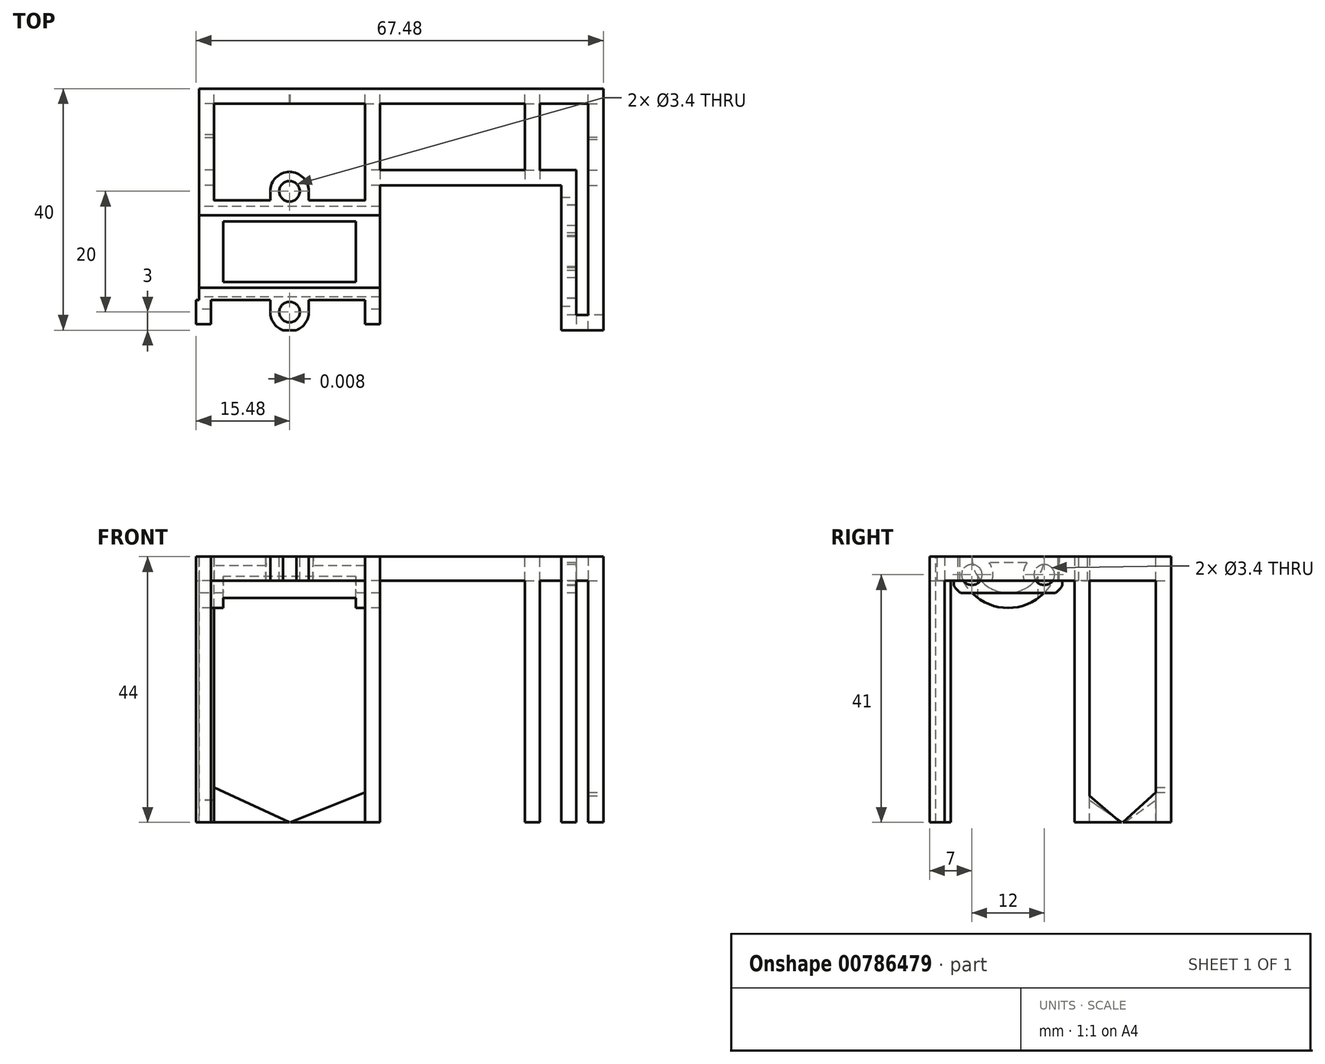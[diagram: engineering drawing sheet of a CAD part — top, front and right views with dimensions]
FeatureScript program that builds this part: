
annotation { "Feature Type Name" : "Feature", "Feature Type Description" : "" }
export const myFeature = defineFeature(function(context is Context, id is Id, definition is map)
    precondition{}
    {
        {
            var Q0;
            Q0=qCreatedBy(makeId("Top.planeOp"),FACE);
            var sketch = newSketch(context, id + "F0", { "sketchPlane" : qUnion([Q0])});
            skLineSegment(sketch, "E0.bottom", {"start": v(-33.5, 20) * mm, "end": v(33.5, 20) * mm});
            skLineSegment(sketch, "E0.top", {"start": v(-33.5, -20) * mm, "end": v(-3.5, -20) * mm});
            skLineSegment(sketch, "E0.left", {"start": v(-33.5, 20) * mm, "end": v(-33.5, -20) * mm});
            skLineSegment(sketch, "E0.right", {"start": v(33.5, 20) * mm, "end": v(33.5, -20) * mm});
            skLineSegment(sketch, "E1.top", {"start": v(-3.5, 4) * mm, "end": v(26.5, 4) * mm});
            skLineSegment(sketch, "E1.left", {"start": v(-3.5, -20) * mm, "end": v(-3.5, 4) * mm});
            skLineSegment(sketch, "E1.right", {"start": v(26.5, -20) * mm, "end": v(26.5, 4) * mm});
            skLineSegment(sketch, "E2.trimOffspring", {"start": v(26.5, -20) * mm, "end": v(33.5, -20) * mm});
            skSolve(sketch);
        }
        {
            var Q0;
            Q0 = qSketchRegion(id + "F0", true);
            extrude(context, id + "F1", {"entities" : qUnion([Q0]), "depth" : 4 * mm, "offsetDistance" : 25 * mm});
        }
        {
            var Q0;
            Q0=makeQuery(id+"F1.opExtrude","SWEPT_FACE",FACE,{"disambiguationData":[OSD([sQuery(id+"F0.wireOp",EDGE,"E0.left")])]});
            var sketch = newSketch(context, id + "F2", { "sketchPlane" : qUnion([Q0])});
            skArc(sketch, "E3", {"start": v(1, 4) * mm, "mid": v(7, -2) * mm, "end": v(13, 4) * mm});
            skArc(sketch, "E4", {"start": v(-1.5, 4) * mm, "mid": v(7, -4.5) * mm, "end": v(15.5, 4) * mm});
            skLineSegment(sketch, "E5", {"start": v(-1.5, 4) * mm, "end": v(15.5, 4) * mm});
            skSolve(sketch);
        }
        {
            var Q0;
            {var subQ0=sQuery(id+"F2.wireOp",EDGE,"E3");var subQ1=makeQuery(id+"F1.opExtrude","CAP_EDGE",EDGE,{"disambiguationData":[OSD([sQuery(id+"F0.wireOp",EDGE,"E0.left")])],"isStart":true});var subQ2=makeQuery(id+"F2.imprint","INTERSECT",VERTEX,{"disambiguationData":[OD(0.0)],"derivedFrom":[subQ1,subQ0]});Q0=makeQuery(id+"F2.imprint","IMPRINT",FACE,{"disambiguationData":[TD([[makeQuery(id+"F2.imprint","IMPRINT",EDGE,{"disambiguationData":[TD([[subQ2,-1.0]])],"derivedFrom":subQ0}),-1.0]])]});}
            extrude(context, id + "F3", {"entities" : qUnion([Q0]), "operationType" : NewBodyOperationType.ADD, "oppositeDirection" : true, "depth" : 30 * mm, "offsetDistance" : 25 * mm});
        }
        {
            var Q0;
            {var subQ0=sQuery(id+"F2.wireOp",EDGE,"E5");var subQ1=sQuery(id+"F2.wireOp",EDGE,"E3");var subQ2=makeQuery(id+"F2.imprint","INTERSECT",VERTEX,{"disambiguationData":[OD(0.0)],"derivedFrom":[subQ1,subQ0]});Q0=makeQuery(id+"F2.imprint","IMPRINT",FACE,{"disambiguationData":[TD([[makeQuery(id+"F2.imprint","IMPRINT",EDGE,{"disambiguationData":[TD([[subQ2,-1.0]])],"derivedFrom":subQ1}),1.0]])]});}
            extrude(context, id + "F4", {"entities" : qUnion([Q0]), "operationType" : NewBodyOperationType.REMOVE, "oppositeDirection" : true, "depth" : 30 * mm, "offsetDistance" : 25 * mm});
        }
        {
            var Q0;
            {var subQ0=sQuery(id+"F0.wireOp",EDGE,"E1.left");var subQ1=sQuery(id+"F0.wireOp",EDGE,"E0.left");var subQ5=sQuery(id+"F0.wireOp",EDGE,"E0.top");Q0=makeQuery(id+"F4.boolean.opBoolean","SPLIT",FACE,{"disambiguationData":[TD([makeQuery(id+"F1.opExtrude","SWEPT_FACE",FACE,{"disambiguationData":[OSD([subQ5])]})])],"derivedFrom":makeQuery(id+"F1.opExtrude","CAP_FACE",FACE,{"disambiguationData":[OSD([sQuery(id+"F0.wireOp",EDGE,"E0.bottom"),subQ5,subQ1,sQuery(id+"F0.wireOp",EDGE,"E0.right"),sQuery(id+"F0.wireOp",EDGE,"E1.top"),subQ0,sQuery(id+"F0.wireOp",EDGE,"E1.right"),sQuery(id+"F0.wireOp",EDGE,"E2.trimOffspring")])],"isStart":false})});}
            var sketch = newSketch(context, id + "F5", { "sketchPlane" : qUnion([Q0])});
            skCircle(sketch, "E6", {"center": v(-18.5, -17) * mm, "radius": 1.7 * mm});
            skSolve(sketch);
        }
        {
            var Q0;
            Q0 = qSketchRegion(id + "F5", true);
            extrude(context, id + "F6", {"entities" : qUnion([Q0]), "operationType" : NewBodyOperationType.REMOVE, "oppositeDirection" : true, "depth" : 4 * mm, "offsetDistance" : 25 * mm});
        }
        {
            var Q0;
            {var subQ2=sQuery(id+"F0.wireOp",EDGE,"E0.left");var subQ3=sQuery(id+"F0.wireOp",EDGE,"E1.top");var subQ4=sQuery(id+"F0.wireOp",EDGE,"E0.right");var subQ5=sQuery(id+"F0.wireOp",EDGE,"E2.trimOffspring");var subQ6=sQuery(id+"F0.wireOp",EDGE,"E1.right");var subQ7=sQuery(id+"F0.wireOp",EDGE,"E1.left");var subQ8=sQuery(id+"F0.wireOp",EDGE,"E0.bottom");Q0=makeQuery(id+"F4.boolean.opBoolean","SPLIT",FACE,{"disambiguationData":[TD([makeQuery(id+"F1.opExtrude","SWEPT_FACE",FACE,{"disambiguationData":[OSD([subQ8])]})])],"derivedFrom":makeQuery(id+"F1.opExtrude","CAP_FACE",FACE,{"disambiguationData":[OSD([subQ8,sQuery(id+"F0.wireOp",EDGE,"E0.top"),subQ2,subQ4,subQ3,subQ7,subQ6,subQ5])],"isStart":false})});}
            var sketch = newSketch(context, id + "F7", { "sketchPlane" : qUnion([Q0])});
            skCircle(sketch, "E7", {"center": v(-18.5, 3) * mm, "radius": 1.7 * mm});
            skSolve(sketch);
        }
        {
            var Q0;
            Q0 = qSketchRegion(id + "F7", true);
            extrude(context, id + "F8", {"entities" : qUnion([Q0]), "operationType" : NewBodyOperationType.REMOVE, "endBound" : BoundingType.THROUGH_ALL, "oppositeDirection" : true, "depth" : 70 * mm, "offsetDistance" : 25 * mm});
        }
        {
            var Q0;
            {var subQ2=sQuery(id+"F0.wireOp",EDGE,"E0.left");var subQ3=sQuery(id+"F0.wireOp",EDGE,"E1.top");var subQ4=sQuery(id+"F0.wireOp",EDGE,"E0.right");var subQ5=sQuery(id+"F0.wireOp",EDGE,"E2.trimOffspring");var subQ6=sQuery(id+"F0.wireOp",EDGE,"E1.right");var subQ7=sQuery(id+"F0.wireOp",EDGE,"E1.left");var subQ8=sQuery(id+"F0.wireOp",EDGE,"E0.bottom");Q0=makeQuery(id+"F4.boolean.opBoolean","SPLIT",FACE,{"disambiguationData":[TD([makeQuery(id+"F1.opExtrude","SWEPT_FACE",FACE,{"disambiguationData":[OSD([subQ8])]})])],"derivedFrom":makeQuery(id+"F1.opExtrude","CAP_FACE",FACE,{"disambiguationData":[OSD([subQ8,sQuery(id+"F0.wireOp",EDGE,"E0.top"),subQ2,subQ4,subQ3,subQ7,subQ6,subQ5])],"isStart":false})});}
            shell(context, id + "F9", {"entities" : qUnion([Q0]), "thickness" : 2.5 * mm});
        }
        {
            var Q0;
            Q0=makeQuery(id+"F9.opShell","OFFSET_FACE",FACE,{"disambiguationData":[OSD([sQuery(id+"F0.wireOp",EDGE,"E0.bottom"),sQuery(id+"F0.wireOp",EDGE,"E0.top"),sQuery(id+"F0.wireOp",EDGE,"E0.left"),sQuery(id+"F0.wireOp",EDGE,"E0.right"),sQuery(id+"F0.wireOp",EDGE,"E1.top"),sQuery(id+"F0.wireOp",EDGE,"E1.left"),sQuery(id+"F0.wireOp",EDGE,"E1.right"),sQuery(id+"F0.wireOp",EDGE,"E2.trimOffspring")])]});
            extrude(context, id + "F10", {"entities" : qUnion([Q0]), "operationType" : NewBodyOperationType.REMOVE, "oppositeDirection" : true, "depth" : 3 * mm, "offsetDistance" : 25 * mm});
        }
        {
            var Q0;
            {var subQ0=sQuery(id+"F0.wireOp",EDGE,"E1.left");var subQ1=sQuery(id+"F0.wireOp",EDGE,"E0.left");var subQ5=sQuery(id+"F0.wireOp",EDGE,"E0.top");Q0=makeQuery(id+"F4.boolean.opBoolean","SPLIT",FACE,{"disambiguationData":[TD([makeQuery(id+"F1.opExtrude","SWEPT_FACE",FACE,{"disambiguationData":[OSD([subQ5])]})])],"derivedFrom":makeQuery(id+"F1.opExtrude","CAP_FACE",FACE,{"disambiguationData":[OSD([sQuery(id+"F0.wireOp",EDGE,"E0.bottom"),subQ5,subQ1,sQuery(id+"F0.wireOp",EDGE,"E0.right"),sQuery(id+"F0.wireOp",EDGE,"E1.top"),subQ0,sQuery(id+"F0.wireOp",EDGE,"E1.right"),sQuery(id+"F0.wireOp",EDGE,"E2.trimOffspring")])],"isStart":false})});}
            var sketch = newSketch(context, id + "F11", { "sketchPlane" : qUnion([Q0])});
            skLineSegment(sketch, "E8.bottom", {"start": v(-7.5, -2) * mm, "end": v(-29.5, -2) * mm});
            skLineSegment(sketch, "E8.top", {"start": v(-7.5, -12) * mm, "end": v(-29.5, -12) * mm});
            skLineSegment(sketch, "E8.left", {"start": v(-7.5, -2) * mm, "end": v(-7.5, -12) * mm});
            skLineSegment(sketch, "E8.right", {"start": v(-29.5, -2) * mm, "end": v(-29.5, -12) * mm});
            skSolve(sketch);
        }
        {
            var Q0;
            Q0 = qSketchRegion(id + "F11", true);
            extrude(context, id + "F12", {"entities" : qUnion([Q0]), "operationType" : NewBodyOperationType.REMOVE, "oppositeDirection" : true, "depth" : 9 * mm, "offsetDistance" : 25 * mm});
        }
        {
            var Q0;
            Q0=makeQuery(id+"F1.opExtrude","SWEPT_FACE",FACE,{"disambiguationData":[OSD([sQuery(id+"F0.wireOp",EDGE,"E1.right")])]});
            var sketch = newSketch(context, id + "F13", { "sketchPlane" : qUnion([Q0])});
            skLineSegment(sketch, "E9.bottom", {"start": v(16, -3) * mm, "end": v(-2, -3) * mm});
            skLineSegment(sketch, "E9.top", {"start": v(16, 7) * mm, "end": v(-2, 7) * mm});
            skLineSegment(sketch, "E9.left", {"start": v(16, -3) * mm, "end": v(16, 7) * mm});
            skLineSegment(sketch, "E9.right", {"start": v(-2, -3) * mm, "end": v(-2, 7) * mm});
            skSolve(sketch);
        }
        {
            var Q0;
            Q0 = qSketchRegion(id + "F13", true);
            extrude(context, id + "F14", {"entities" : qUnion([Q0]), "operationType" : NewBodyOperationType.ADD, "oppositeDirection" : true, "depth" : 2.5 * mm, "offsetDistance" : 25 * mm});
        }
        {
            var Q0;
            Q0=makeQuery(id+"F14.boolean.opBoolean","MERGE",FACE,{"derivedFrom":[makeQuery(id+"F1.opExtrude","SWEPT_FACE",FACE,{"disambiguationData":[OSD([sQuery(id+"F0.wireOp",EDGE,"E1.right")])]}),makeQuery(id+"F14.opExtrude","CAP_FACE",FACE,{"disambiguationData":[OSD([sQuery(id+"F13.wireOp",EDGE,"E9.bottom"),sQuery(id+"F13.wireOp",EDGE,"E9.top"),sQuery(id+"F13.wireOp",EDGE,"E9.left"),sQuery(id+"F13.wireOp",EDGE,"E9.right")])],"isStart":true})]});
            var sketch = newSketch(context, id + "F15", { "sketchPlane" : qUnion([Q0])});
            skCircle(sketch, "E10", {"center": v(1, 1) * mm, "radius": 1.7 * mm});
            skCircle(sketch, "E11", {"center": v(13, 1) * mm, "radius": 1.7 * mm});
            skLineSegment(sketch, "E12.bottom", {"start": v(-2, 4) * mm, "end": v(16, 4) * mm});
            skLineSegment(sketch, "E12.top", {"start": v(-2, 7) * mm, "end": v(16, 7) * mm});
            skLineSegment(sketch, "E12.left", {"start": v(-2, 4) * mm, "end": v(-2, 7) * mm});
            skLineSegment(sketch, "E12.right", {"start": v(16, 4) * mm, "end": v(16, 7) * mm});
            skSolve(sketch);
        }
        {
            var Q0;
            Q0 = qSketchRegion(id + "F15", true);
            extrude(context, id + "F16", {"entities" : qUnion([Q0]), "operationType" : NewBodyOperationType.REMOVE, "oppositeDirection" : true, "depth" : 2.5 * mm, "offsetDistance" : 25 * mm});
        }
        {
            var Q0;
            Q0=makeQuery(id+"F14.boolean.opBoolean","MERGE",FACE,{"derivedFrom":[makeQuery(id+"F1.opExtrude","SWEPT_FACE",FACE,{"disambiguationData":[OSD([sQuery(id+"F0.wireOp",EDGE,"E1.right")])]}),makeQuery(id+"F14.opExtrude","CAP_FACE",FACE,{"disambiguationData":[OSD([sQuery(id+"F13.wireOp",EDGE,"E9.bottom"),sQuery(id+"F13.wireOp",EDGE,"E9.top"),sQuery(id+"F13.wireOp",EDGE,"E9.left"),sQuery(id+"F13.wireOp",EDGE,"E9.right")])],"isStart":true})]});
            var sketch = newSketch(context, id + "F17", { "sketchPlane" : qUnion([Q0])});
            skCircle(sketch, "E13", {"center": v(1, 1) * mm, "radius": 3.5 * mm});
            skCircle(sketch, "E14", {"center": v(13, 1) * mm, "radius": 3.5 * mm});
            skLineSegment(sketch, "E15", {"start": v(1, -2.5) * mm, "end": v(13, -2.5) * mm});
            skLineSegment(sketch, "E16", {"start": v(1, 4.5) * mm, "end": v(13, 4.5) * mm});
            skLineSegment(sketch, "E17", {"start": v(-2, 3) * mm, "end": v(-1.87, 3) * mm});
            skLineSegment(sketch, "E18", {"start": v(-2.35, 0) * mm, "end": v(-2, 0) * mm});
            skLineSegment(sketch, "E19", {"start": v(16.1, 3) * mm, "end": v(15.88, 2.99) * mm});
            skLineSegment(sketch, "E20", {"start": v(16.35, 0) * mm, "end": v(16, 0) * mm});
            skLineSegment(sketch, "E21", {"start": v(4.35, 0) * mm, "end": v(9.65, 0) * mm});
            skLineSegment(sketch, "E22", {"start": v(3.87, 3) * mm, "end": v(10.13, 3) * mm});
            skSolve(sketch);
        }
        {
            var Q0;
            {var subQ0=sQuery(id+"F17.wireOp",EDGE,"E15");Q0=makeQuery(id+"F17.imprint","IMPRINT",FACE,{"disambiguationData":[TD([[makeQuery(id+"F17.imprint","IMPRINT",EDGE,{"derivedFrom":subQ0}),-1.0]])]});}
            var Q1;
            {var subQ1=sQuery(id+"F17.wireOp",EDGE,"E16");Q1=makeQuery(id+"F17.imprint","IMPRINT",FACE,{"disambiguationData":[TD([[makeQuery(id+"F17.imprint","IMPRINT",EDGE,{"derivedFrom":subQ1}),1.0]])]});}
            var Q2;
            {var subQ0=sQuery(id+"F17.wireOp",EDGE,"E21");Q2=makeQuery(id+"F17.imprint","IMPRINT",FACE,{"disambiguationData":[TD([[makeQuery(id+"F17.imprint","IMPRINT",EDGE,{"derivedFrom":subQ0}),1.0]])]});}
            extrude(context, id + "F18", {"entities" : qUnion([Q0, Q1, Q2]), "operationType" : NewBodyOperationType.REMOVE, "oppositeDirection" : true, "depth" : 2.5 * mm, "offsetDistance" : 25 * mm});
        }
        {
            var Q0;
            {var subQ2=sQuery(id+"F0.wireOp",EDGE,"E0.left");var subQ3=sQuery(id+"F0.wireOp",EDGE,"E1.top");var subQ4=sQuery(id+"F0.wireOp",EDGE,"E0.right");var subQ5=sQuery(id+"F0.wireOp",EDGE,"E2.trimOffspring");var subQ6=sQuery(id+"F0.wireOp",EDGE,"E1.right");var subQ7=sQuery(id+"F0.wireOp",EDGE,"E1.left");var subQ8=sQuery(id+"F0.wireOp",EDGE,"E0.bottom");Q0=makeQuery(id+"F18.boolean.opBoolean","MERGE",FACE,{"derivedFrom":[makeQuery(id+"F4.boolean.opBoolean","SPLIT",FACE,{"disambiguationData":[TD([makeQuery(id+"F1.opExtrude","SWEPT_FACE",FACE,{"disambiguationData":[OSD([subQ8])]})])],"derivedFrom":makeQuery(id+"F1.opExtrude","CAP_FACE",FACE,{"disambiguationData":[OSD([subQ8,sQuery(id+"F0.wireOp",EDGE,"E0.top"),subQ2,subQ4,subQ3,subQ7,subQ6,subQ5])],"isStart":false})}),makeQuery(id+"F18.opExtrude","SWEPT_FACE",FACE,{"disambiguationData":[OSD([sQuery(id+"F17.wireOp",EDGE,"E17")])]})]});}
            var sketch = newSketch(context, id + "F19", { "sketchPlane" : qUnion([Q0])});
            skLineSegment(sketch, "E23", {"start": v(-6, 6.5) * mm, "end": v(-6, 17.5) * mm});
            skLineSegment(sketch, "E24", {"start": v(-3.5, 6.5) * mm, "end": v(-3.5, 17.5) * mm});
            skLineSegment(sketch, "E25", {"start": v(20.5, 6.5) * mm, "end": v(20.5, 17.5) * mm});
            skLineSegment(sketch, "E26", {"start": v(23, 6.5) * mm, "end": v(23, 17.5) * mm});
            skSolve(sketch);
        }
        {
            var Q0;
            {var subQ0=sQuery(id+"F19.wireOp",EDGE,"E23");Q0=makeQuery(id+"F19.imprint","IMPRINT",FACE,{"disambiguationData":[TD([[makeQuery(id+"F19.imprint","IMPRINT",EDGE,{"derivedFrom":subQ0}),-1.0]])]});}
            var Q1;
            {var subQ0=sQuery(id+"F19.wireOp",EDGE,"E25");Q1=makeQuery(id+"F19.imprint","IMPRINT",FACE,{"disambiguationData":[TD([[makeQuery(id+"F19.imprint","IMPRINT",EDGE,{"derivedFrom":subQ0}),-1.0]])]});}
            extrude(context, id + "F20", {"entities" : qUnion([Q0, Q1]), "operationType" : NewBodyOperationType.ADD, "oppositeDirection" : true, "depth" : 4 * mm, "offsetDistance" : 25 * mm});
        }
        {
            var Q0;
            {var subQ0=sQuery(id+"F0.wireOp",EDGE,"E1.left");var subQ1=sQuery(id+"F0.wireOp",EDGE,"E0.left");var subQ5=sQuery(id+"F0.wireOp",EDGE,"E0.top");Q0=makeQuery(id+"F4.boolean.opBoolean","SPLIT",FACE,{"disambiguationData":[TD([makeQuery(id+"F1.opExtrude","SWEPT_FACE",FACE,{"disambiguationData":[OSD([subQ5])]})])],"derivedFrom":makeQuery(id+"F1.opExtrude","CAP_FACE",FACE,{"disambiguationData":[OSD([sQuery(id+"F0.wireOp",EDGE,"E0.bottom"),subQ5,subQ1,sQuery(id+"F0.wireOp",EDGE,"E0.right"),sQuery(id+"F0.wireOp",EDGE,"E1.top"),subQ0,sQuery(id+"F0.wireOp",EDGE,"E1.right"),sQuery(id+"F0.wireOp",EDGE,"E2.trimOffspring")])],"isStart":false})});}
            var sketch = newSketch(context, id + "F21", { "sketchPlane" : qUnion([Q0])});
            skArc(sketch, "E27", {"start": v(-17.38, -20) * mm, "mid": v(-18.5, -13.8) * mm, "end": v(-19.6, -20) * mm});
            skLineSegment(sketch, "E28", {"start": v(-21.7, -17) * mm, "end": v(-21.7, -13) * mm});
            skLineSegment(sketch, "E29", {"start": v(-15.3, -17) * mm, "end": v(-15.3, -13) * mm});
            skLineSegment(sketch, "E30", {"start": v(-21.7, -15) * mm, "end": v(-33.5, -15) * mm});
            skLineSegment(sketch, "E31", {"start": v(-15.3, -15) * mm, "end": v(-3.5, -15) * mm});
            skLineSegment(sketch, "E32", {"start": v(-19.6, -20) * mm, "end": v(-17.38, -20) * mm});
            skSolve(sketch);
        }
        {
            var Q0;
            {var subQ12=sQuery(id+"F21.wireOp",EDGE,"E30");Q0=makeQuery(id+"F21.imprint","IMPRINT",FACE,{"disambiguationData":[TD([[makeQuery(id+"F21.imprint","IMPRINT",EDGE,{"derivedFrom":subQ12}),1.0]])]});}
            var Q1;
            {var subQ11=sQuery(id+"F21.wireOp",EDGE,"E31");Q1=makeQuery(id+"F21.imprint","IMPRINT",FACE,{"disambiguationData":[TD([[makeQuery(id+"F21.imprint","IMPRINT",EDGE,{"derivedFrom":subQ11}),-1.0]])]});}
            extrude(context, id + "F22", {"entities" : qUnion([Q0, Q1]), "operationType" : NewBodyOperationType.REMOVE, "oppositeDirection" : true, "depth" : 4 * mm, "offsetDistance" : 25 * mm});
        }
        {
            var Q0;
            {var subQ0=sQuery(id+"F0.wireOp",EDGE,"E1.top");var subQ1=sQuery(id+"F0.wireOp",EDGE,"E0.bottom");var subQ4=sQuery(id+"F0.wireOp",EDGE,"E0.left");var subQ5=sQuery(id+"F0.wireOp",EDGE,"E0.right");var subQ6=sQuery(id+"F0.wireOp",EDGE,"E2.trimOffspring");var subQ7=sQuery(id+"F0.wireOp",EDGE,"E1.right");var subQ8=sQuery(id+"F0.wireOp",EDGE,"E1.left");Q0=makeQuery(id+"F20.boolean.opBoolean","MERGE",FACE,{"derivedFrom":[makeQuery(id+"F18.boolean.opBoolean","MERGE",FACE,{"derivedFrom":[makeQuery(id+"F4.boolean.opBoolean","SPLIT",FACE,{"disambiguationData":[TD([makeQuery(id+"F1.opExtrude","SWEPT_FACE",FACE,{"disambiguationData":[OSD([subQ1])]})])],"derivedFrom":makeQuery(id+"F1.opExtrude","CAP_FACE",FACE,{"disambiguationData":[OSD([subQ1,sQuery(id+"F0.wireOp",EDGE,"E0.top"),subQ4,subQ5,subQ0,subQ8,subQ7,subQ6])],"isStart":false})}),makeQuery(id+"F18.opExtrude","SWEPT_FACE",FACE,{"disambiguationData":[OSD([sQuery(id+"F17.wireOp",EDGE,"E17")])]})]}),makeQuery(id+"F20.opExtrude","CAP_FACE",FACE,{"disambiguationData":[OSD([subQ1,subQ0,sQuery(id+"F19.wireOp",EDGE,"E23"),sQuery(id+"F19.wireOp",EDGE,"E24")])],"isStart":true}),makeQuery(id+"F20.opExtrude","CAP_FACE",FACE,{"disambiguationData":[OSD([subQ1,subQ0,sQuery(id+"F19.wireOp",EDGE,"E25"),sQuery(id+"F19.wireOp",EDGE,"E26")])],"isStart":true})]});}
            var sketch = newSketch(context, id + "F23", { "sketchPlane" : qUnion([Q0])});
            skCircle(sketch, "E33", {"center": v(-18.5, 3) * mm, "radius": 3.2 * mm});
            skLineSegment(sketch, "E34", {"start": v(-14.58, 1.5) * mm, "end": v(-15.3, 1.5) * mm});
            skLineSegment(sketch, "E35", {"start": v(-15.3, 3) * mm, "end": v(-15.3, 1.5) * mm});
            skPoint(sketch, "E35.endSnap0", {"position": v(-15.13, 1.5) * mm});
            skLineSegment(sketch, "E36", {"start": v(-22.42, 1.5) * mm, "end": v(-21.7, 1.5) * mm});
            skLineSegment(sketch, "E37", {"start": v(-21.7, 3) * mm, "end": v(-21.7, 1.5) * mm});
            skPoint(sketch, "E37.endSnap0", {"position": v(-21.87, 1.5) * mm});
            skPoint(sketch, "E38.orphan", {"position": v(-21.33, 1.5) * mm});
            skPoint(sketch, "E39.orphan", {"position": v(-15.67, 1.5) * mm});
            skSolve(sketch);
        }
        {
            var Q0;
            Q0=makeQuery(id+"F23.imprint","IMPRINT",FACE,{"disambiguationData":[TD([[makeQuery(id+"F23.imprint","IMPRINT",EDGE,{"derivedFrom":sQuery(id+"F23.wireOp",EDGE,"E34")}),-1.0]])]});
            extrude(context, id + "F24", {"entities" : qUnion([Q0]), "operationType" : NewBodyOperationType.REMOVE, "oppositeDirection" : true, "depth" : 4 * mm, "offsetDistance" : 25 * mm});
        }
        {
            var Q0;
            Q0=makeQuery(id+"F15.imprint","IMPRINT",FACE,{"disambiguationData":[TD([[makeQuery(id+"F15.imprint","IMPRINT",EDGE,{"derivedFrom":sQuery(id+"F15.wireOp",EDGE,"E12.bottom")}),1.0]])]});
            extrude(context, id + "F25", {"entities" : qUnion([Q0]), "operationType" : NewBodyOperationType.REMOVE, "oppositeDirection" : true, "depth" : 2.5 * mm, "offsetDistance" : 25 * mm});
        }
        {
            var Q0;
            Q0=makeQuery(id+"F14.boolean.opBoolean","MERGE",FACE,{"derivedFrom":[makeQuery(id+"F1.opExtrude","SWEPT_FACE",FACE,{"disambiguationData":[OSD([sQuery(id+"F0.wireOp",EDGE,"E1.right")])]}),makeQuery(id+"F14.opExtrude","CAP_FACE",FACE,{"disambiguationData":[OSD([sQuery(id+"F13.wireOp",EDGE,"E9.bottom"),sQuery(id+"F13.wireOp",EDGE,"E9.top"),sQuery(id+"F13.wireOp",EDGE,"E9.left"),sQuery(id+"F13.wireOp",EDGE,"E9.right")])],"isStart":true})]});
            var sketch = newSketch(context, id + "F26", { "sketchPlane" : qUnion([Q0])});
            skLineSegment(sketch, "E40", {"start": v(-0.72, -2.05) * mm, "end": v(14.72, -2.05) * mm});
            skSolve(sketch);
        }
        {
            var Q0;
            {var subQ0=sQuery(id+"F26.wireOp",EDGE,"E40");Q0=makeQuery(id+"F26.imprint","IMPRINT",FACE,{"disambiguationData":[TD([[makeQuery(id+"F26.imprint","IMPRINT",EDGE,{"derivedFrom":subQ0}),-1.0]])]});}
            extrude(context, id + "F27", {"entities" : qUnion([Q0]), "operationType" : NewBodyOperationType.REMOVE, "oppositeDirection" : true, "depth" : 2.5 * mm, "offsetDistance" : 25 * mm});
        }
        {
            var Q0;
            {var subQ0=sQuery(id+"F0.wireOp",EDGE,"E1.top");var subQ1=sQuery(id+"F0.wireOp",EDGE,"E0.bottom");var subQ2=sQuery(id+"F0.wireOp",EDGE,"E0.left");var subQ4=sQuery(id+"F0.wireOp",EDGE,"E0.right");var subQ5=sQuery(id+"F0.wireOp",EDGE,"E1.left");var subQ6=sQuery(id+"F0.wireOp",EDGE,"E1.right");var subQ7=sQuery(id+"F0.wireOp",EDGE,"E2.trimOffspring");Q0=makeQuery(id+"F20.boolean.opBoolean","MERGE",FACE,{"derivedFrom":[makeQuery(id+"F3.boolean.opBoolean","SPLIT",FACE,{"disambiguationData":[TD([makeQuery(id+"F1.opExtrude","SWEPT_FACE",FACE,{"disambiguationData":[OSD([subQ1])]})])],"derivedFrom":makeQuery(id+"F1.opExtrude","CAP_FACE",FACE,{"disambiguationData":[OSD([subQ1,sQuery(id+"F0.wireOp",EDGE,"E0.top"),subQ2,subQ4,subQ0,subQ5,subQ6,subQ7])],"isStart":true})}),makeQuery(id+"F20.opExtrude","CAP_FACE",FACE,{"disambiguationData":[OSD([subQ1,subQ0,sQuery(id+"F19.wireOp",EDGE,"E23"),sQuery(id+"F19.wireOp",EDGE,"E24")])],"isStart":false}),makeQuery(id+"F20.opExtrude","CAP_FACE",FACE,{"disambiguationData":[OSD([subQ1,subQ0,sQuery(id+"F19.wireOp",EDGE,"E25"),sQuery(id+"F19.wireOp",EDGE,"E26")])],"isStart":false})]});}
            var sketch = newSketch(context, id + "F28", { "sketchPlane" : qUnion([Q0])});
            skLineSegment(sketch, "E41.bottom", {"start": v(-3.5, -6.5) * mm, "end": v(-6, -6.5) * mm});
            skLineSegment(sketch, "E41.top", {"start": v(-3.5, -4) * mm, "end": v(-6, -4) * mm});
            skLineSegment(sketch, "E41.left", {"start": v(-3.5, -6.5) * mm, "end": v(-3.5, -4) * mm});
            skLineSegment(sketch, "E41.right", {"start": v(-6, -6.5) * mm, "end": v(-6, -4) * mm});
            skLineSegment(sketch, "E42.bottom", {"start": v(20.5, -6.5) * mm, "end": v(23, -6.5) * mm});
            skLineSegment(sketch, "E42.top", {"start": v(20.5, -4) * mm, "end": v(23, -4) * mm});
            skLineSegment(sketch, "E42.left", {"start": v(20.5, -6.5) * mm, "end": v(20.5, -4) * mm});
            skLineSegment(sketch, "E42.right", {"start": v(23, -6.5) * mm, "end": v(23, -4) * mm});
            skLineSegment(sketch, "E43.bottom", {"start": v(20.5, -17.5) * mm, "end": v(23, -17.5) * mm});
            skLineSegment(sketch, "E43.top", {"start": v(20.5, -20) * mm, "end": v(23, -20) * mm});
            skLineSegment(sketch, "E43.left", {"start": v(20.5, -17.5) * mm, "end": v(20.5, -20) * mm});
            skLineSegment(sketch, "E43.right", {"start": v(23, -17.5) * mm, "end": v(23, -20) * mm});
            skLineSegment(sketch, "E44.bottom", {"start": v(-6, -17.5) * mm, "end": v(-3.5, -17.5) * mm});
            skLineSegment(sketch, "E44.top", {"start": v(-6, -20) * mm, "end": v(-3.5, -20) * mm});
            skLineSegment(sketch, "E44.left", {"start": v(-6, -17.5) * mm, "end": v(-6, -20) * mm});
            skLineSegment(sketch, "E44.right", {"start": v(-3.5, -17.5) * mm, "end": v(-3.5, -20) * mm});
            skLineSegment(sketch, "E45.bottom", {"start": v(-31, -17.5) * mm, "end": v(-33.5, -17.5) * mm});
            skLineSegment(sketch, "E45.top", {"start": v(-31, -20) * mm, "end": v(-33.5, -20) * mm});
            skLineSegment(sketch, "E45.left", {"start": v(-31, -17.5) * mm, "end": v(-31, -20) * mm});
            skLineSegment(sketch, "E45.right", {"start": v(-33.5, -17.5) * mm, "end": v(-33.5, -20) * mm});
            skLineSegment(sketch, "E46.bottom", {"start": v(-31, -4) * mm, "end": v(-33.5, -4) * mm});
            skLineSegment(sketch, "E46.top", {"start": v(-31, -6.5) * mm, "end": v(-33.5, -6.5) * mm});
            skLineSegment(sketch, "E46.left", {"start": v(-31, -4) * mm, "end": v(-31, -6.5) * mm});
            skLineSegment(sketch, "E46.right", {"start": v(-33.5, -4) * mm, "end": v(-33.5, -6.5) * mm});
            skLineSegment(sketch, "E47.bottom", {"start": v(31, -6.5) * mm, "end": v(33.5, -6.5) * mm});
            skLineSegment(sketch, "E47.top", {"start": v(31, -4) * mm, "end": v(33.5, -4) * mm});
            skLineSegment(sketch, "E47.left", {"start": v(31, -6.5) * mm, "end": v(31, -4) * mm});
            skLineSegment(sketch, "E47.right", {"start": v(33.5, -6.5) * mm, "end": v(33.5, -4) * mm});
            skLineSegment(sketch, "E48.bottom", {"start": v(31, -17.5) * mm, "end": v(33.5, -17.5) * mm});
            skLineSegment(sketch, "E48.top", {"start": v(31, -20) * mm, "end": v(33.5, -20) * mm});
            skLineSegment(sketch, "E48.left", {"start": v(31, -17.5) * mm, "end": v(31, -20) * mm});
            skLineSegment(sketch, "E48.right", {"start": v(33.5, -17.5) * mm, "end": v(33.5, -20) * mm});
            skLineSegment(sketch, "E49.bottom", {"start": v(33.5, 20) * mm, "end": v(31, 20) * mm});
            skLineSegment(sketch, "E49.top", {"start": v(33.5, 17.5) * mm, "end": v(31, 17.5) * mm});
            skLineSegment(sketch, "E49.left", {"start": v(33.5, 20) * mm, "end": v(33.5, 17.5) * mm});
            skLineSegment(sketch, "E49.right", {"start": v(31, 20) * mm, "end": v(31, 17.5) * mm});
            skLineSegment(sketch, "E50.bottom", {"start": v(29, 17.5) * mm, "end": v(26.5, 17.5) * mm});
            skLineSegment(sketch, "E50.top", {"start": v(29, 20) * mm, "end": v(26.5, 20) * mm});
            skLineSegment(sketch, "E50.left", {"start": v(29, 17.5) * mm, "end": v(29, 20) * mm});
            skLineSegment(sketch, "E50.right", {"start": v(26.5, 17.5) * mm, "end": v(26.5, 20) * mm});
            skSolve(sketch);
        }
        {
            var Q0;
            Q0 = qSketchRegion(id + "F28", true);
            extrude(context, id + "F29", {"entities" : qUnion([Q0]), "operationType" : NewBodyOperationType.ADD, "depth" : 40 * mm, "offsetDistance" : 25 * mm});
        }
        {
            var Q0;
            Q0=makeQuery(id+"F22.boolean.opBoolean","COPY",FACE,{"derivedFrom":makeQuery(id+"F22.opExtrude","SWEPT_FACE",FACE,{"disambiguationData":[OSD([sQuery(id+"F21.wireOp",EDGE,"E31")])]})});
            var sketch = newSketch(context, id + "F30", { "sketchPlane" : qUnion([Q0])});
            skLineSegment(sketch, "E51.bottom", {"start": v(-3.5, 4) * mm, "end": v(-6, 4) * mm});
            skLineSegment(sketch, "E51.top", {"start": v(-3.5, 0) * mm, "end": v(-6, 0) * mm});
            skLineSegment(sketch, "E51.left", {"start": v(-3.5, 4) * mm, "end": v(-3.5, 0) * mm});
            skLineSegment(sketch, "E51.right", {"start": v(-6, 4) * mm, "end": v(-6, 0) * mm});
            skLineSegment(sketch, "E52.bottom", {"start": v(-33.98, 4) * mm, "end": v(-31.48, 4) * mm});
            skLineSegment(sketch, "E52.top", {"start": v(-33.98, 0) * mm, "end": v(-31.48, 0) * mm});
            skLineSegment(sketch, "E52.left", {"start": v(-33.98, 4) * mm, "end": v(-33.98, 0) * mm});
            skLineSegment(sketch, "E52.right", {"start": v(-31.48, 4) * mm, "end": v(-31.48, 0) * mm});
            skSolve(sketch);
        }
        {
            var Q0;
            Q0 = qSketchRegion(id + "F30", true);
            extrude(context, id + "F31", {"entities" : qUnion([Q0]), "operationType" : NewBodyOperationType.ADD, "depth" : 4 * mm, "offsetDistance" : 25 * mm});
        }
        {
            var Q0;
            {var subQ0=sQuery(id+"F0.wireOp",EDGE,"E1.left");var subQ3=sQuery(id+"F0.wireOp",EDGE,"E0.left");var subQ4=sQuery(id+"F0.wireOp",EDGE,"E0.top");Q0=makeQuery(id+"F31.boolean.opBoolean","MERGE",FACE,{"derivedFrom":[makeQuery(id+"F3.boolean.opBoolean","SPLIT",FACE,{"disambiguationData":[TD([makeQuery(id+"F1.opExtrude","SWEPT_FACE",FACE,{"disambiguationData":[OSD([subQ4])]})])],"derivedFrom":makeQuery(id+"F1.opExtrude","CAP_FACE",FACE,{"disambiguationData":[OSD([sQuery(id+"F0.wireOp",EDGE,"E0.bottom"),subQ4,subQ3,sQuery(id+"F0.wireOp",EDGE,"E0.right"),sQuery(id+"F0.wireOp",EDGE,"E1.top"),subQ0,sQuery(id+"F0.wireOp",EDGE,"E1.right"),sQuery(id+"F0.wireOp",EDGE,"E2.trimOffspring")])],"isStart":true})}),makeQuery(id+"F31.opExtrude","SWEPT_FACE",FACE,{"disambiguationData":[OSD([sQuery(id+"F30.wireOp",EDGE,"E51.top")])]}),makeQuery(id+"F31.opExtrude","SWEPT_FACE",FACE,{"disambiguationData":[OSD([sQuery(id+"F30.wireOp",EDGE,"E52.top")])]})]});}
            var sketch = newSketch(context, id + "F32", { "sketchPlane" : qUnion([Q0])});
            skLineSegment(sketch, "E53.bottom", {"start": v(-6, 19) * mm, "end": v(-3.5, 19) * mm});
            skLineSegment(sketch, "E54.bottom", {"start": v(-33.98, 19) * mm, "end": v(-31.48, 19) * mm});
            skLineSegment(sketch, "E55", {"start": v(-3.5, 16.5) * mm, "end": v(-6, 16.5) * mm});
            skLineSegment(sketch, "E56", {"start": v(-31.48, 16.5) * mm, "end": v(-33.98, 16.5) * mm});
            skSolve(sketch);
        }
        {
            var Q0;
            {var subQ0=sQuery(id+"F32.wireOp",EDGE,"E54.bottom");Q0=makeQuery(id+"F32.imprint","IMPRINT",FACE,{"disambiguationData":[TD([[makeQuery(id+"F32.imprint","IMPRINT",EDGE,{"derivedFrom":subQ0}),-1.0]])]});}
            var Q1;
            {var subQ0=sQuery(id+"F32.wireOp",EDGE,"E53.bottom");Q1=makeQuery(id+"F32.imprint","IMPRINT",FACE,{"disambiguationData":[TD([[makeQuery(id+"F32.imprint","IMPRINT",EDGE,{"derivedFrom":subQ0}),-1.0]])]});}
            extrude(context, id + "F33", {"entities" : qUnion([Q0, Q1]), "operationType" : NewBodyOperationType.ADD, "depth" : 40 * mm, "offsetDistance" : 25 * mm});
        }
        {
            var Q0;
            Q0=makeQuery(id+"F29.boolean.opBoolean","MERGE",FACE,{"derivedFrom":[makeQuery(id+"F1.opExtrude","SWEPT_FACE",FACE,{"disambiguationData":[OSD([sQuery(id+"F0.wireOp",EDGE,"E0.bottom")])]}),makeQuery(id+"F29.opExtrude","SWEPT_FACE",FACE,{"disambiguationData":[OSD([sQuery(id+"F28.wireOp",EDGE,"E43.top")])]}),makeQuery(id+"F29.opExtrude","SWEPT_FACE",FACE,{"disambiguationData":[OSD([sQuery(id+"F28.wireOp",EDGE,"E44.top")])]}),makeQuery(id+"F29.opExtrude","SWEPT_FACE",FACE,{"disambiguationData":[OSD([sQuery(id+"F28.wireOp",EDGE,"E45.top")])]}),makeQuery(id+"F29.opExtrude","SWEPT_FACE",FACE,{"disambiguationData":[OSD([sQuery(id+"F28.wireOp",EDGE,"E48.top")])]})]});
            var sketch = newSketch(context, id + "F34", { "sketchPlane" : qUnion([Q0])});
            skLineSegment(sketch, "E57", {"start": v(31, -34.22) * mm, "end": v(18.5, -40) * mm});
            skLineSegment(sketch, "E58", {"start": v(3.5, -34.22) * mm, "end": v(-8.5, -40) * mm});
            skLineSegment(sketch, "E59", {"start": v(-23, -34.22) * mm, "end": v(-27.5, -40) * mm});
            skLineSegment(sketch, "E60", {"start": v(-8.5, -40) * mm, "end": v(3.5, -40) * mm});
            skLineSegment(sketch, "E61", {"start": v(-20.5, -34.33) * mm, "end": v(-8.9, -40) * mm});
            skLineSegment(sketch, "E62", {"start": v(-8.9, -40) * mm, "end": v(-20.5, -40) * mm});
            skLineSegment(sketch, "E63", {"start": v(-23, -40) * mm, "end": v(-27.5, -40) * mm});
            skLineSegment(sketch, "E64", {"start": v(31, -40) * mm, "end": v(18.5, -40) * mm});
            skLineSegment(sketch, "E65", {"start": v(6, -35.04) * mm, "end": v(18.38, -40) * mm});
            skLineSegment(sketch, "E66", {"start": v(6, -40) * mm, "end": v(18.38, -40) * mm});
            skSolve(sketch);
        }
        {
            var Q0;
            Q0=makeQuery(id+"F29.boolean.opBoolean","MERGE",FACE,{"derivedFrom":[makeQuery(id+"F1.opExtrude","SWEPT_FACE",FACE,{"disambiguationData":[OSD([sQuery(id+"F0.wireOp",EDGE,"E0.right")])]}),makeQuery(id+"F29.opExtrude","SWEPT_FACE",FACE,{"disambiguationData":[OSD([sQuery(id+"F28.wireOp",EDGE,"E47.right")])]}),makeQuery(id+"F29.opExtrude","SWEPT_FACE",FACE,{"disambiguationData":[OSD([sQuery(id+"F28.wireOp",EDGE,"E48.right")])]}),makeQuery(id+"F29.opExtrude","SWEPT_FACE",FACE,{"disambiguationData":[OSD([sQuery(id+"F28.wireOp",EDGE,"E49.left")])]})]});
            var sketch = newSketch(context, id + "F35", { "sketchPlane" : qUnion([Q0])});
            skLineSegment(sketch, "E67", {"start": v(12, -40) * mm, "end": v(17.5, -35.06) * mm});
            skLineSegment(sketch, "E68", {"start": v(17.5, -40) * mm, "end": v(12, -40) * mm});
            skSolve(sketch);
        }
        {
            var Q0;
            {var subQ4=sQuery(id+"F35.wireOp",EDGE,"E67");Q0=makeQuery(id+"F35.imprint","IMPRINT",FACE,{"disambiguationData":[TD([[makeQuery(id+"F35.imprint","IMPRINT",EDGE,{"derivedFrom":subQ4}),-1.0]])]});}
            var Q1;
            {var subQ4=sQuery(id+"F35.wireOp",EDGE,"BmQwMLFp-4yRf-Zwj2-MiTX-SXmsMWruuArx");Q1=makeQuery(id+"F35.imprint","IMPRINT",FACE,{"disambiguationData":[TD([[makeQuery(id+"F35.imprint","IMPRINT",EDGE,{"derivedFrom":subQ4}),1.0]])]});}
            extrude(context, id + "F36", {"entities" : qUnion([Q0, Q1]), "operationType" : NewBodyOperationType.ADD, "oppositeDirection" : true, "depth" : 2.5 * mm, "offsetDistance" : 25 * mm});
        }
        {
            var Q0;
            {var subQ4=sQuery(id+"F35.wireOp",EDGE,"E67");Q0=makeQuery(id+"F35.imprint","IMPRINT",FACE,{"disambiguationData":[TD([[makeQuery(id+"F35.imprint","IMPRINT",EDGE,{"derivedFrom":subQ4}),-1.0]])]});}
            extrude(context, id + "F37", {"entities" : qUnion([Q0]), "operationType" : NewBodyOperationType.ADD, "oppositeDirection" : true, "depth" : 2.5 * mm, "offsetDistance" : 25 * mm});
        }
        {
            var Q0;
            {var subQ0=sQuery(id+"F28.wireOp",EDGE,"E48.right");var subQ1=sQuery(id+"F0.wireOp",EDGE,"E0.right");Q0=makeQuery(id+"F36.boolean.opBoolean","MERGE",FACE,{"derivedFrom":[makeQuery(id+"F29.boolean.opBoolean","MERGE",FACE,{"derivedFrom":[makeQuery(id+"F1.opExtrude","SWEPT_FACE",FACE,{"disambiguationData":[OSD([subQ1])]}),makeQuery(id+"F29.opExtrude","SWEPT_FACE",FACE,{"disambiguationData":[OSD([sQuery(id+"F28.wireOp",EDGE,"E47.right")])]}),makeQuery(id+"F29.opExtrude","SWEPT_FACE",FACE,{"disambiguationData":[OSD([subQ0])]}),makeQuery(id+"F29.opExtrude","SWEPT_FACE",FACE,{"disambiguationData":[OSD([sQuery(id+"F28.wireOp",EDGE,"E49.left")])]})]}),makeQuery(id+"F36.opExtrude","CAP_FACE",FACE,{"disambiguationData":[OSD([subQ1,sQuery(id+"F28.wireOp",EDGE,"E48.bottom"),subQ0,sQuery(id+"F35.wireOp",EDGE,"E67"),sQuery(id+"F35.wireOp",EDGE,"E68")])],"isStart":true})]});}
            var sketch = newSketch(context, id + "F38", { "sketchPlane" : qUnion([Q0])});
            skLineSegment(sketch, "E69", {"start": v(6.5, -35.6) * mm, "end": v(11.61, -40) * mm});
            skLineSegment(sketch, "E70", {"start": v(11.61, -40) * mm, "end": v(6.5, -40) * mm});
            skSolve(sketch);
        }
        {
            var Q0;
            {var subQ0=sQuery(id+"F38.wireOp",EDGE,"E69");Q0=makeQuery(id+"F38.imprint","IMPRINT",FACE,{"disambiguationData":[TD([[makeQuery(id+"F38.imprint","IMPRINT",EDGE,{"derivedFrom":subQ0}),-1.0]])]});}
            extrude(context, id + "F39", {"entities" : qUnion([Q0]), "operationType" : NewBodyOperationType.ADD, "oppositeDirection" : true, "depth" : 2.5 * mm, "offsetDistance" : 25 * mm});
        }
        {
            var Q0;
            {var subQ0=sQuery(id+"F34.wireOp",EDGE,"E65");Q0=makeQuery(id+"F34.imprint","IMPRINT",FACE,{"disambiguationData":[TD([[makeQuery(id+"F34.imprint","IMPRINT",EDGE,{"derivedFrom":subQ0}),-1.0]])]});}
            var Q1;
            {var subQ0=sQuery(id+"F34.wireOp",EDGE,"E57");Q1=makeQuery(id+"F34.imprint","IMPRINT",FACE,{"disambiguationData":[TD([[makeQuery(id+"F34.imprint","IMPRINT",EDGE,{"derivedFrom":subQ0}),1.0]])]});}
            extrude(context, id + "F40", {"entities" : qUnion([Q0, Q1]), "operationType" : NewBodyOperationType.ADD, "oppositeDirection" : true, "depth" : 2.5 * mm, "offsetDistance" : 25 * mm});
        }
        {
            var Q0;
            {var subQ0=sQuery(id+"F0.wireOp",EDGE,"E0.left");Q0=makeQuery(id+"F29.boolean.opBoolean","MERGE",FACE,{"derivedFrom":[makeQuery(id+"F3.boolean.opBoolean","MERGE",FACE,{"derivedFrom":[makeQuery(id+"F1.opExtrude","SWEPT_FACE",FACE,{"disambiguationData":[OSD([subQ0])]}),makeQuery(id+"F3.opExtrude","CAP_FACE",FACE,{"disambiguationData":[OSD([subQ0,sQuery(id+"F2.wireOp",EDGE,"E3"),sQuery(id+"F2.wireOp",EDGE,"E4")])],"isStart":true})]}),makeQuery(id+"F29.opExtrude","SWEPT_FACE",FACE,{"disambiguationData":[OSD([sQuery(id+"F28.wireOp",EDGE,"E45.right")])]}),makeQuery(id+"F29.opExtrude","SWEPT_FACE",FACE,{"disambiguationData":[OSD([sQuery(id+"F28.wireOp",EDGE,"E46.right")])]})]});}
            var sketch = newSketch(context, id + "F41", { "sketchPlane" : qUnion([Q0])});
            skLineSegment(sketch, "E71", {"start": v(-6.5, -40) * mm, "end": v(-11.85, -40) * mm});
            skLineSegment(sketch, "E72", {"start": v(-11.85, -40) * mm, "end": v(-6.5, -36.38) * mm});
            skLineSegment(sketch, "E73", {"start": v(-17.5, -40) * mm, "end": v(-12.35, -40) * mm});
            skLineSegment(sketch, "E74", {"start": v(-12.35, -40) * mm, "end": v(-17.5, -36.32) * mm});
            skSolve(sketch);
        }
        {
            var Q0;
            {var subQ0=sQuery(id+"F41.wireOp",EDGE,"E71");Q0=makeQuery(id+"F41.imprint","IMPRINT",FACE,{"disambiguationData":[TD([[makeQuery(id+"F41.imprint","IMPRINT",EDGE,{"derivedFrom":subQ0}),-1.0]])]});}
            var Q1;
            {var subQ0=sQuery(id+"F41.wireOp",EDGE,"E73");Q1=makeQuery(id+"F41.imprint","IMPRINT",FACE,{"disambiguationData":[TD([[makeQuery(id+"F41.imprint","IMPRINT",EDGE,{"derivedFrom":subQ0}),1.0]])]});}
            extrude(context, id + "F42", {"entities" : qUnion([Q0, Q1]), "operationType" : NewBodyOperationType.ADD, "oppositeDirection" : true, "depth" : 2.5 * mm, "offsetDistance" : 25 * mm});
        }
    });
